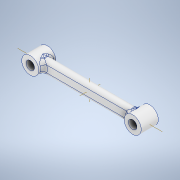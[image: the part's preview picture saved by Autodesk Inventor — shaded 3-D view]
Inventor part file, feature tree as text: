
AUTODESK INVENTOR PART (.ipt)
format: ipt  version: 2021.1 (Build 251245000, 245)  size: 269,824 bytes
history: native  units: in
note: dims shown in document units (in); Inventor stores cm internally (conversion verified against a paired STEP export)
features: fillet x3, extrude x2, sketch x2, projected_geometry x2
ambient origin geometry x8: Origin, YZ Plane, XZ Plane, XY Plane, X Axis, Y Axis, Z Axis, Center Point
bodies: Solid1 (feature_tree)
feature tree (9):
  extrude  "Extrusion1"  Depth=0.5in
  extrude  "Extrusion2"  Depth=0.5in
  fillet  "Fillet1"  Radius=6.0in
  fillet  "Fillet2"  Radius=1.0in
  fillet  "Fillet3"  Radius=0.8in
  sketch  "Sketch1"  dims[d0=1.0in d1=0.5in]
  sketch  "Sketch2"  dims[d2=1.0in d3=0.5in d4=6.0in d5=1.0in d6=0.0in d7=0.8in d8=0.4in d9=0.0in d10=0.4in d11=0.2in d12=0.2in]
  projected_geometry  "Projected Loop1"
  projected_geometry  "Projected Loop2"
